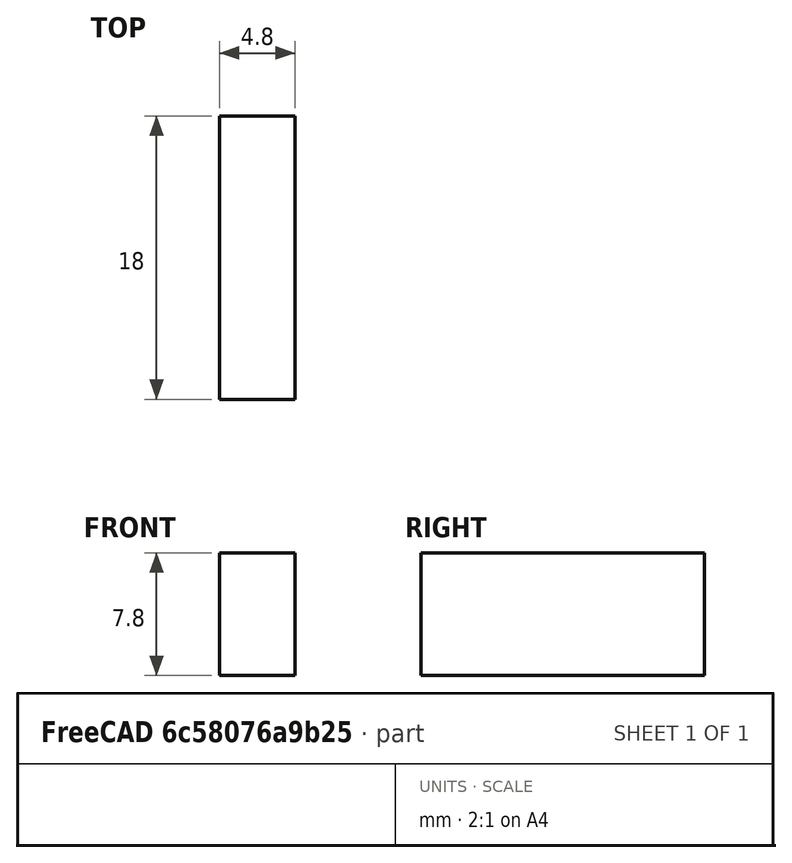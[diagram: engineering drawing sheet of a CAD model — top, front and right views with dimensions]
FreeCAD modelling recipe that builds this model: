
FCSTD DOCUMENT  (FreeCAD 0.18R16117 (Git))
Label: TCM2 -ModuloWIFI 3
License: All rights reserved
LicenseURL: http://en.wikipedia.org/wiki/All_rights_reserved
objects: Sketcher::SketchObject×1, PartDesign::Pad×1, PartDesign::Body×1
note: 4 computed .brp shape members not serialized (recipe doc carries the construction recipe); baked Part::Feature solids carry a one-line shape summary decoded from their .brp

FEATURE [Sketcher::SketchObject] Sketch
  MapMode = 5
  Support = -> [XY_Plane]
  sketch-geometry (4):
    g0: LineSegment StartX=0.414993 StartY=10.7267 StartZ=0 EndX=5.21499 EndY=10.7267 EndZ=0
    g1: LineSegment StartX=5.21499 StartY=10.7267 StartZ=0 EndX=5.21499 EndY=-7.2733 EndZ=0
    g2: LineSegment StartX=5.21499 StartY=-7.2733 StartZ=0 EndX=0.414993 EndY=-7.2733 EndZ=0
    g3: LineSegment StartX=0.414993 StartY=-7.2733 StartZ=0 EndX=0.414993 EndY=10.7267 EndZ=0
  constraints (10):
    c: Coincident(g0,g1)
    c: Coincident(g1,g2)
    c: Coincident(g2,g3)
    c: Coincident(g3,g0)
    c: Horizontal(g0)
    c: Horizontal(g2)
    c: Vertical(g1)
    c: Vertical(g3)
    c: Distance(g0) = 4.8
    c: Distance(g1) = 18
FEATURE [PartDesign::Pad] Pad
  Length = 7.8
  Length2 = 100
  Profile = -> Sketch
  Type = 0
FEATURE [PartDesign::Body] Body
  Group = -> [Sketch,Pad]
  Origin = -> Origin
  Tip = -> Pad
